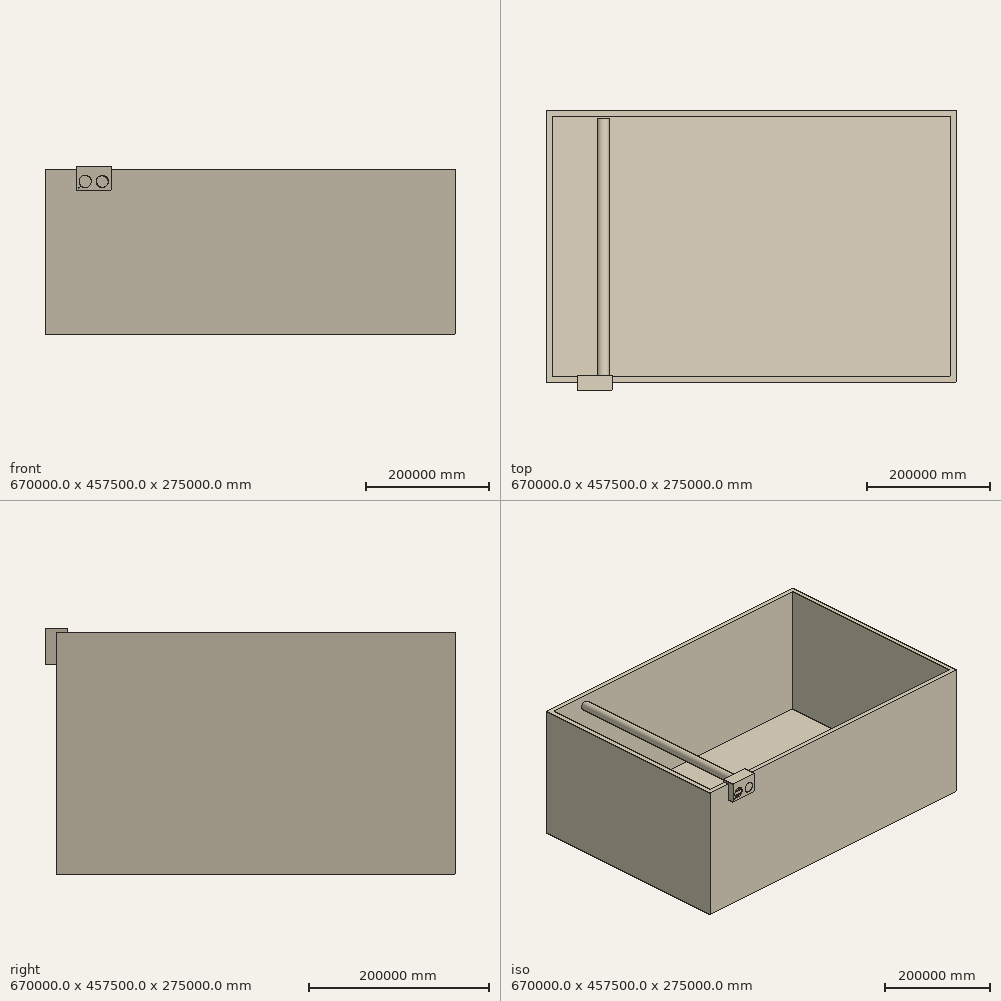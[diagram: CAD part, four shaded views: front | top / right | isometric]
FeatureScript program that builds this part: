
annotation { "Feature Type Name" : "Feature", "Feature Type Description" : "" }
export const myFeature = defineFeature(function(context is Context, id is Id, definition is map)
    precondition{}
    {
        {
            var Q0;
            Q0=qCreatedBy(makeId("Top.planeOp"),FACE);
            var sketch = newSketch(context, id + "F0", { "sketchPlane" : qUnion([Q0])});
            skLineSegment(sketch, "E0.bottom", {"start": v(-335000, 222500) * mm, "end": v(335000, 222500) * mm});
            skLineSegment(sketch, "E0.top", {"start": v(-335000, -222500) * mm, "end": v(335000, -222500) * mm});
            skLineSegment(sketch, "E0.left", {"start": v(-335000, 222500) * mm, "end": v(-335000, -222500) * mm});
            skLineSegment(sketch, "E0.right", {"start": v(335000, 222500) * mm, "end": v(335000, -222500) * mm});
            skPoint(sketch, "E0.middle", {"position": v(0, 0) * mm});
            skSolve(sketch);
        }
        {
            var Q0;
            Q0 = qSketchRegion(id + "F0", true);
            extrude(context, id + "F1", {"entities" : qUnion([Q0]), "oppositeDirection" : true, "depth" : 270000 * mm, "offsetDistance" : 25 * mm});
        }
        {
            var Q0;
            Q0=makeQuery(id+"F1.opExtrude","CAP_FACE",FACE,{"disambiguationData":[OSD([sQuery(id+"F0.wireOp",EDGE,"E0.bottom"),sQuery(id+"F0.wireOp",EDGE,"E0.top"),sQuery(id+"F0.wireOp",EDGE,"E0.left"),sQuery(id+"F0.wireOp",EDGE,"E0.right")])],"isStart":true});
            shell(context, id + "F2", {"entities" : qUnion([Q0]), "thickness" : 10000 * mm});
        }
        {
            var Q0;
            Q0=makeQuery(id+"F1.opExtrude","SWEPT_FACE",FACE,{"disambiguationData":[OSD([sQuery(id+"F0.wireOp",EDGE,"E0.top")])]});
            var sketch = newSketch(context, id + "F3", { "sketchPlane" : qUnion([Q0])});
            skLineSegment(sketch, "E1.bottom", {"start": v(-227000, -35000) * mm, "end": v(-285000, -35000) * mm});
            skLineSegment(sketch, "E1.top", {"start": v(-227000, 5000) * mm, "end": v(-285000, 5000) * mm});
            skLineSegment(sketch, "E1.left", {"start": v(-227000, -35000) * mm, "end": v(-227000, 5000) * mm});
            skLineSegment(sketch, "E1.right", {"start": v(-285000, -35000) * mm, "end": v(-285000, 5000) * mm});
            skPoint(sketch, "E1.middle", {"position": v(-231036.4, 0) * mm});
            skSolve(sketch);
        }
        {
            var Q0;
            Q0 = qSketchRegion(id + "F3", true);
            extrude(context, id + "F4", {"entities" : qUnion([Q0]), "operationType" : NewBodyOperationType.ADD, "endBound" : BoundingType.SYMMETRIC, "oppositeDirection" : true, "depth" : 25000 * mm, "offsetDistance" : 25 * mm});
        }
        {
            var Q0;
            {var subQ2=sQuery(id+"F3.wireOp",EDGE,"E1.bottom");Q0=makeQuery(id+"F4.boolean.opBoolean","SPLIT",FACE,{"disambiguationData":[TD([makeQuery(id+"F1.opExtrude","SWEPT_FACE",FACE,{"disambiguationData":[OSD([sQuery(id+"F0.wireOp",EDGE,"E0.top")])]})])],"derivedFrom":makeQuery(id+"F4.opExtrude","SWEPT_FACE",FACE,{"disambiguationData":[OSD([subQ2])]})});}
            shell(context, id + "F5", {"entities" : qUnion([Q0]), "thickness" : 2000 * mm});
        }
        {
            var Q0;
            Q0=makeQuery(id+"F4.opExtrude","CAP_FACE",FACE,{"disambiguationData":[OSD([sQuery(id+"F3.wireOp",EDGE,"E1.bottom"),sQuery(id+"F3.wireOp",EDGE,"E1.top"),sQuery(id+"F3.wireOp",EDGE,"E1.left"),sQuery(id+"F3.wireOp",EDGE,"E1.right")])],"isStart":true});
            var sketch = newSketch(context, id + "F6", { "sketchPlane" : qUnion([Q0])});
            skCircle(sketch, "E2", {"center": v(-242000, -20000) * mm, "radius": 10000 * mm});
            skCircle(sketch, "E3", {"center": v(-270000, -20000) * mm, "radius": 10000 * mm});
            skCircle(sketch, "E4", {"center": v(-232000, -30000) * mm, "radius": 500 * mm});
            skCircle(sketch, "E5", {"center": v(-280000, -30000) * mm, "radius": 500 * mm});
            skSolve(sketch);
        }
        {
            var Q0;
            Q0 = qSketchRegion(id + "F6", true);
            var Q1;
            Q1=makeQuery(id+"F4.opExtrude","CAP_FACE",FACE,{"disambiguationData":[OSD([sQuery(id+"F3.wireOp",EDGE,"E1.bottom"),sQuery(id+"F3.wireOp",EDGE,"E1.top"),sQuery(id+"F3.wireOp",EDGE,"E1.left"),sQuery(id+"F3.wireOp",EDGE,"E1.right")])],"isStart":false});
            extrude(context, id + "F7", {"entities" : qUnion([Q0]), "operationType" : NewBodyOperationType.REMOVE, "endBound" : BoundingType.UP_TO_SURFACE, "oppositeDirection" : true, "depth" : 25 * mm, "endBoundEntityFace" : qUnion([Q1]), "offsetDistance" : 25 * mm});
        }
        {
            var Q0;
            Q0=makeQuery(id+"F4.opExtrude","CAP_FACE",FACE,{"disambiguationData":[OSD([sQuery(id+"F3.wireOp",EDGE,"E1.bottom"),sQuery(id+"F3.wireOp",EDGE,"E1.top"),sQuery(id+"F3.wireOp",EDGE,"E1.left"),sQuery(id+"F3.wireOp",EDGE,"E1.right")])],"isStart":true});
            var sketch = newSketch(context, id + "F8", { "sketchPlane" : qUnion([Q0])});
            skCircle(sketch, "E6", {"center": v(-242000, -20000) * mm, "radius": 9500 * mm});
            skSolve(sketch);
        }
        {
            var Q0;
            Q0 = qSketchRegion(id + "F8", true);
            extrude(context, id + "F9", {"entities" : qUnion([Q0]), "operationType" : NewBodyOperationType.ADD, "oppositeDirection" : true, "depth" : 445000 * mm, "offsetDistance" : 25 * mm});
        }
        {
            var Q0;
            Q0=makeQuery(id+"F2.opShell","OFFSET_FACE",FACE,{"disambiguationData":[OSD([sQuery(id+"F0.wireOp",EDGE,"E0.top")])]});
            cPlane(context, id + "F10", {"entities" : qUnion([Q0]), "cplaneType" : CPlaneType.OFFSET, "offset" : 210000 * mm, "width" : 150 * mm, "height" : 150 * mm});
        }
    });
